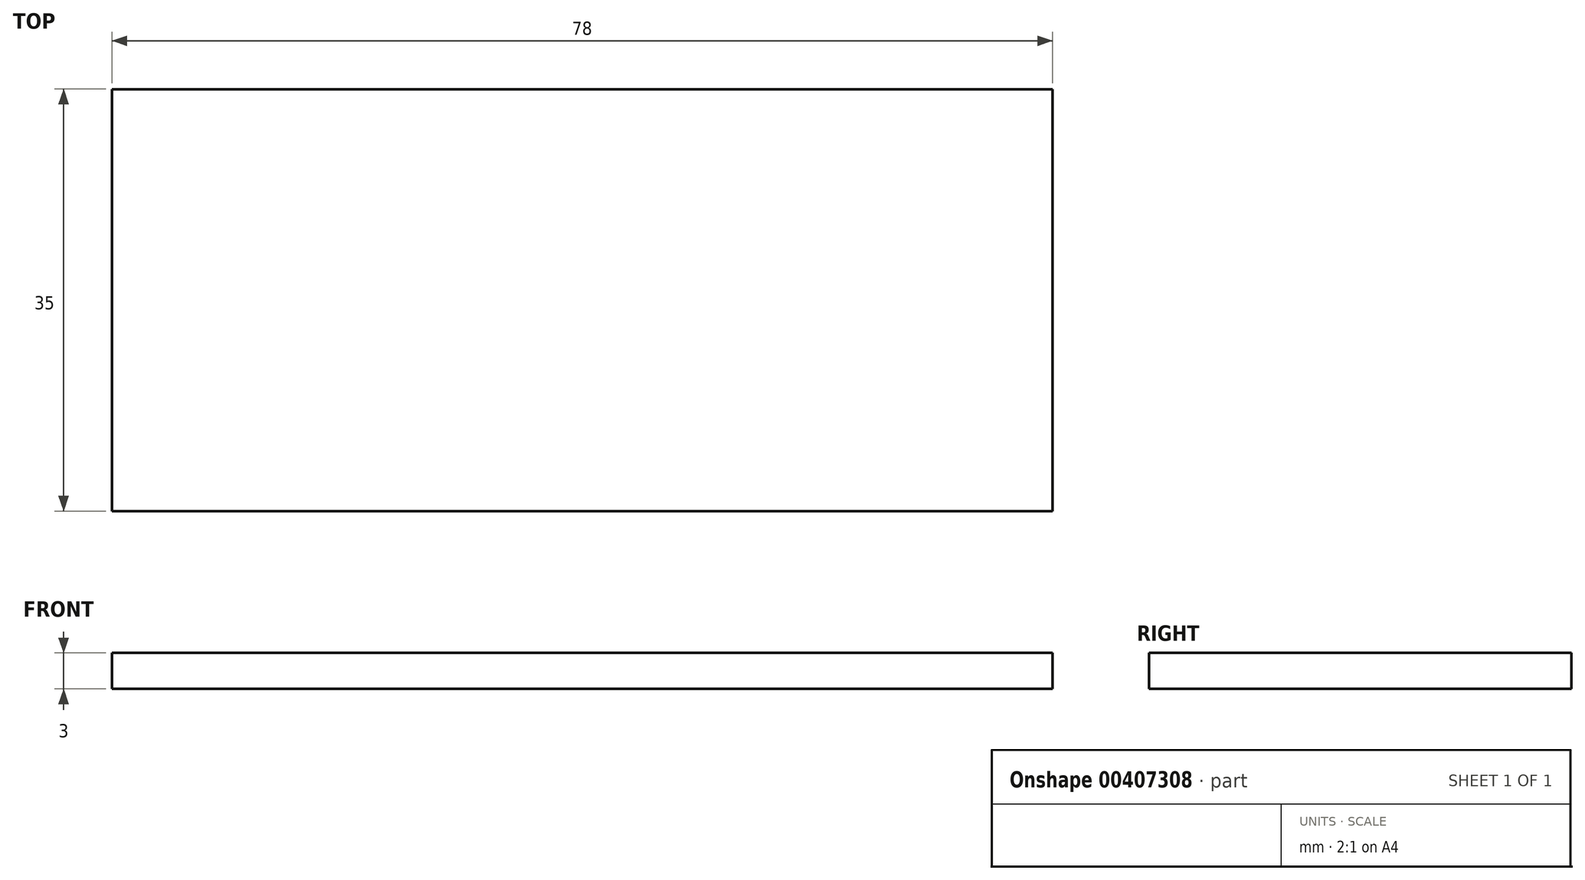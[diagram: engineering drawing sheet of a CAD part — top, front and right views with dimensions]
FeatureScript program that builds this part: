
annotation { "Feature Type Name" : "Feature", "Feature Type Description" : "" }
export const myFeature = defineFeature(function(context is Context, id is Id, definition is map)
    precondition{}
    {
        {
            var Q0;
            Q0=qCreatedBy(makeId("Top.planeOp"),FACE);
            var sketch = newSketch(context, id + "F0", { "sketchPlane" : qUnion([Q0])});
            skLineSegment(sketch, "E0.bottom", {"start": v(0, -1.27) * mm, "end": v(78, -1.27) * mm});
            skLineSegment(sketch, "E0.top", {"start": v(0, -36.27) * mm, "end": v(78, -36.27) * mm});
            skLineSegment(sketch, "E0.left", {"start": v(0, -1.27) * mm, "end": v(0, -36.27) * mm});
            skLineSegment(sketch, "E0.right", {"start": v(78, -1.27) * mm, "end": v(78, -36.27) * mm});
            skSolve(sketch);
        }
        {
            var Q0;
            Q0 = qSketchRegion(id + "F0", true);
            var Q1;
            Q1=makeQuery(id+"F0.imprint","IMPRINT",FACE,{"disambiguationData":[TD([[makeQuery(id+"F0.imprint","IMPRINT",EDGE,{"derivedFrom":sQuery(id+"F0.wireOp",EDGE,"E0.bottom")}),-1.0]])]});
            extrude(context, id + "F1", {"entities" : qUnion([Q0, Q1]), "depth" : 3 * mm});
        }
    });
